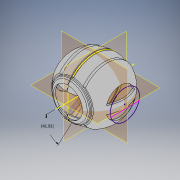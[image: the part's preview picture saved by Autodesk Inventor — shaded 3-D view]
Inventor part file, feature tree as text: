
AUTODESK INVENTOR PART (.ipt)
format: ipt  version: 2019 (Build 230136000, 136)  size: 380,416 bytes
history: native  units: in
note: dims shown in document units (in); Inventor stores cm internally (conversion verified against a paired STEP export)
features: sketch x16, plane x7, extrude x7, revolve x5, mirror x3, projected_geometry x2, shell x1, chamfer x1
ambient origin geometry x8: Origin, YZ Plane, XZ Plane, XY Plane, X Axis, Y Axis, Z Axis, Center Point
bodies: Solid1 (feature_tree)
feature tree (42):
  revolve  "Revolution1"  Angle=90.0deg
  plane  "Work Plane1"
  extrude  "Extrusion1"  Depth=3.0in
  shell  "Shell2"  Thickness=3.0in
  plane  "Work Plane2"
  extrude  "Extrusion2"  Depth=0.2in
  chamfer  "Chamfer1"  Distance=1.125in
  plane  "Work Plane3"
  extrude  "Extrusion3"  Depth=3.15in
  extrude  "Extrusion4"  Depth=1.5in TaperAngle=0.0deg
  extrude  "Extrusion5"  Depth=3.1in
  revolve  "Revolution2"  [1 undecoded]
  mirror  "Mirror1"
  mirror  "Mirror2"
  extrude  "Extrusion6"  Depth=3.0in
  plane  "Work Plane4"
  plane  "Work Plane5"
  extrude  "Extrusion7"  Depth=0.8in
  mirror  "Mirror3"
  revolve  "Revolution3"  [1 undecoded]
  sketch  "Sketch13"  dims[d31=3.0in d32=-3.125in d33=3.0in]
  sketch  "Sketch14"  dims[d34=0.4in d35=0.8in]
  sketch  "Sketch18"  dims[d36=1.8125in d37=0.0in d39=5.8in]
  plane  "Work Plane7"
  revolve  "Revolution5"  [1 undecoded]
  sketch  "Sketch20"  dims[d50=0.025in d51=2.0958in]
  plane  "Work Plane8"
  revolve  "Revolution6"  [1 undecoded]
  sketch  "Sketch1"  dims[d0=6.0in d1=90.0deg]
  sketch  "Sketch2"  dims[d2=3.0in d5=1.0in d7=3.0in]
  sketch  "Sketch3"  dims[d8=1.625in d9=0.0in d11=0.2in]
  sketch  "Sketch4"  dims[d12=-0.25in]
  sketch  "Sketch5"  dims[d13=3.0in]
  sketch  "Sketch6"  dims[d14=4.0in d15=1.125in d16=0.0in]
  projected_geometry  "Projected Loop1"
  sketch  "Sketch7"  dims[d17=0.5in d18=0.125in d19=0.2542in d20=3.15in]
  sketch  "Sketch8"  dims[d21=2.4375in d22=0.0in d23=1.5in d24=0.0in]
  sketch  "Sketch11"  dims[d25=3.9375in d26=0.0in d27=3.1in]
  sketch  "Sketch12"  dims[d28=90.0deg d29=5.0625in d30=0.0in]
  sketch  "Sketch19"  dims[d40=285.0deg d49=0.05in]
  sketch  "Sketch21"  dims[d52=0.2873in d53=6.0in d54=0.1in d55=0.125in d56=0.11in d57=1.8991in d58=0.25in]
  projected_geometry  "Projected Loop2"
note: 4 required parameter values undecoded (feature->parameter linkage not recoverable at this tier; creation-order binding heuristic only, values carry confidence <= 0.55)
